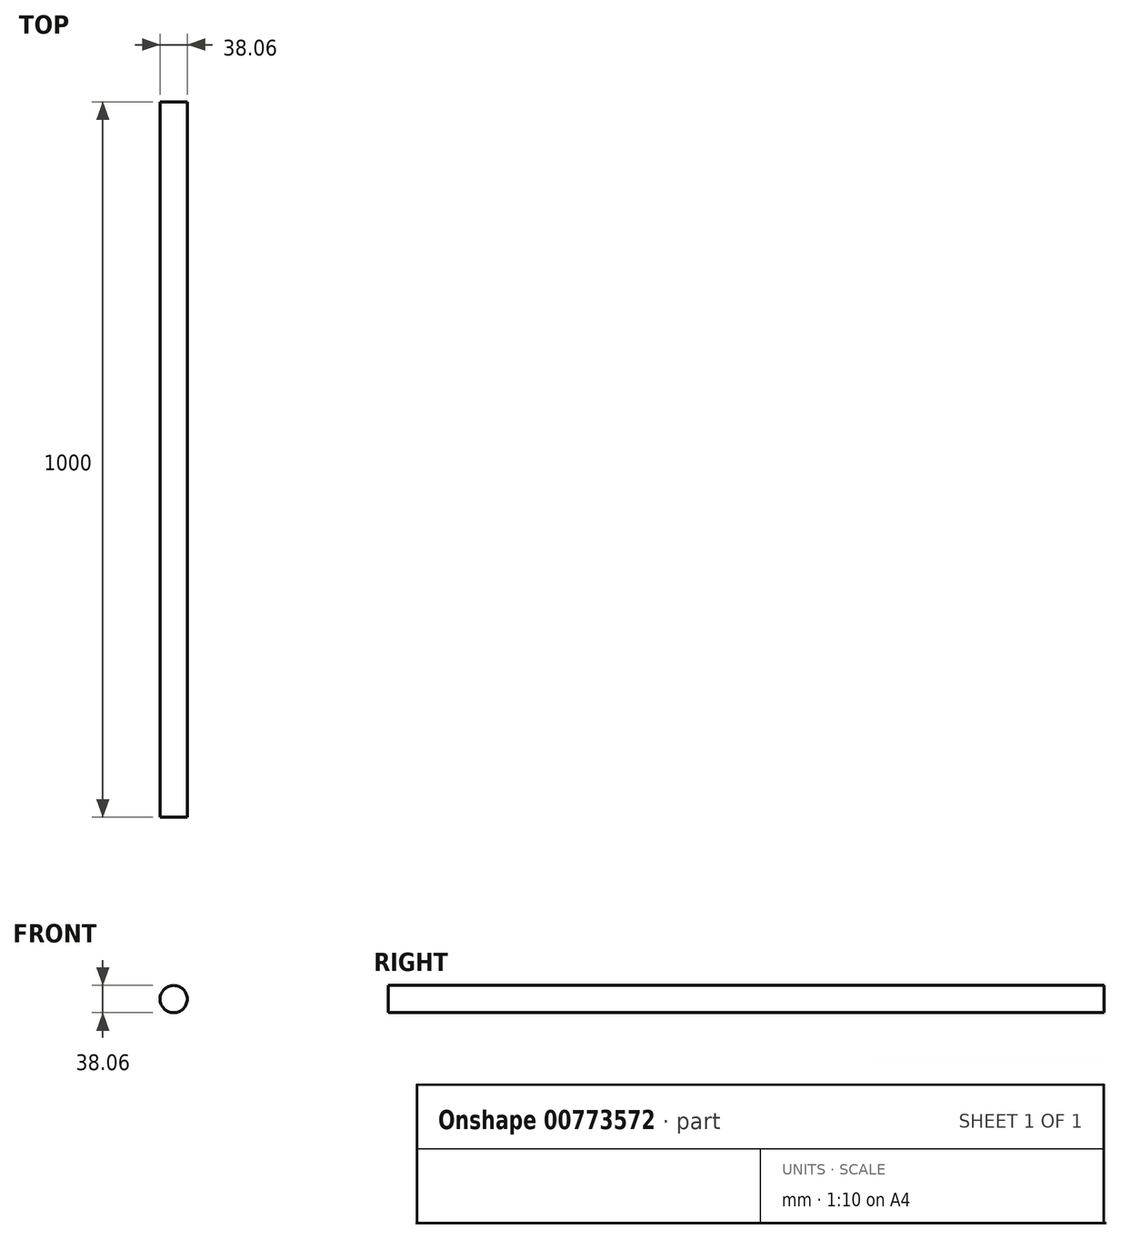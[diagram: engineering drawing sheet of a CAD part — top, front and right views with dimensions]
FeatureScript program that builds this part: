
annotation { "Feature Type Name" : "Feature", "Feature Type Description" : "" }
export const myFeature = defineFeature(function(context is Context, id is Id, definition is map)
    precondition{}
    {
        {
            var Q0;
            Q0=qCreatedBy(makeId("Front.planeOp"),FACE);
            var sketch = newSketch(context, id + "F0", { "sketchPlane" : qUnion([Q0])});
            skCircle(sketch, "E0", {"center": v(0, 0) * mm, "radius": 19.03 * mm});
            skSolve(sketch);
        }
        {
            var Q0;
            Q0 = qSketchRegion(id + "F0", true);
            extrude(context, id + "F1", {"entities" : qUnion([Q0]), "oppositeDirection" : true, "depth" : 500 * mm, "offsetDistance" : 25.4 * mm, "hasSecondDirection" : true, "secondDirectionOppositeDirection" : false, "secondDirectionDepth" : 500 * mm});
        }
        {
            var Q0;
            Q0=makeQuery(id+"F1.opExtrude","SWEPT_BODY",BODY,{"disambiguationData":[OSD([sQuery(id+"F0.wireOp",EDGE,"E0")])]});
            transform(context, id + "F2", {"entities" : qUnion([Q0]), "transformType" : TransformType.TRANSLATION_3D, "dx" : 0 * mm, "dy" : 0 * mm, "dz" : 0 * mm, "makeCopy" : true});
        }
    });
